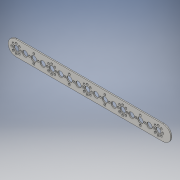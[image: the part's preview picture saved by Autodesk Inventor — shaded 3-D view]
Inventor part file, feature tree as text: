
AUTODESK INVENTOR PART (.ipt)
format: ipt  version: 2016 (Build 200138000, 138)  size: 228,352 bytes
history: native  units: in
note: dims shown in document units (in); Inventor stores cm internally (conversion verified against a paired STEP export)
features: sketch x3, extrude x2, hole x2, fillet x1, pattern_linear x1
ambient origin geometry x8: Origin, YZ Plane, XZ Plane, XY Plane, X Axis, Y Axis, Z Axis, Center Point
bodies: Solid1 (feature_tree)
feature tree (9):
  extrude  "Extrusion1"  Depth=1.063in
  extrude  "Extrusion2"  Depth=0.0803in
  fillet  "Fillet1"  Radius=0.562in
  hole  "Hole1"  [1 undecoded]
  pattern_linear  "Rectangular Pattern1"  Spacing1=0.1in  [1 undecoded]
  hole  "Hole2"  [1 undecoded]
  sketch  "Sketch1"  dims[d0=11.3386in d1=1.063in]
  sketch  "Sketch2"  dims[d2=0.0803in d3=0.0in d4=0.5023in d5=0.562in]
  sketch  "Sketch3"  dims[d6=0.0in d7=0.3839in d8=0.1in d11=6.6929in d13=0.6193in d14=0.3937in d16=1.0in d18=0.0803in d19=0.0in d20=0.5315in d28=3.1496in d30=360.0deg d32=0.1469in d33=0.75in d34=0.375in d35=0.25in d36=0.5635in d37=1.0in d38=0.8108in d39=0.3096in d40=1.9685in d42=2.4772in d43=0.3096in d44=1.5748in d46=360.0deg d48=0.0in d49=0.6134in d50=1.5748in d52=2.4772in d53=0.3937in d55=1.0in d57=0.1469in d58=0.75in d59=0.375in d60=0.25in d61=0.5635in d62=1.0in d63=0.8108in]
note: 3 required parameter values undecoded (feature->parameter linkage not recoverable at this tier; creation-order binding heuristic only, values carry confidence <= 0.55)
